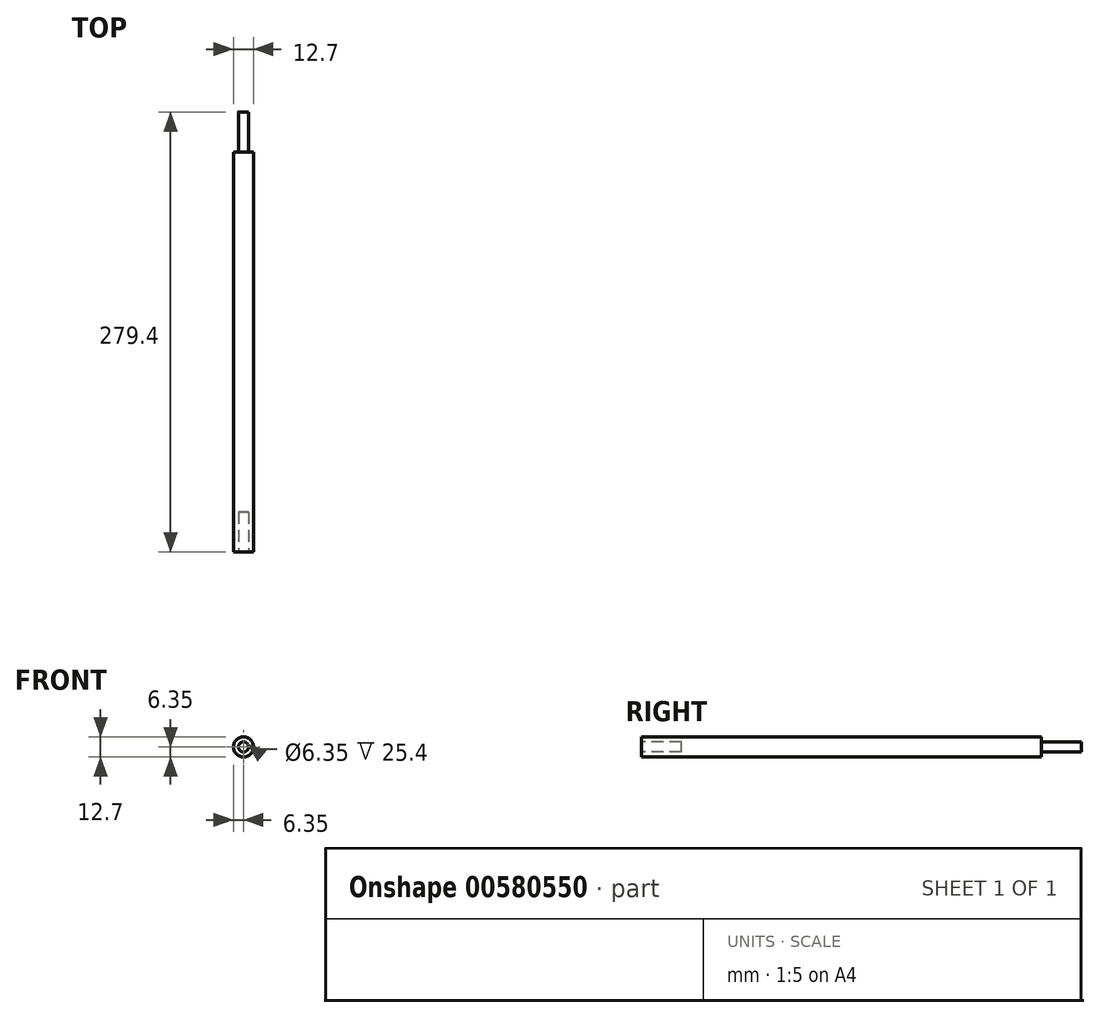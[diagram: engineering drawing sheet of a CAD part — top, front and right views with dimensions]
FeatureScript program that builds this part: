
annotation { "Feature Type Name" : "Feature", "Feature Type Description" : "" }
export const myFeature = defineFeature(function(context is Context, id is Id, definition is map)
    precondition{}
    {
        {
            var Q0;
            Q0=qCreatedBy(makeId("Front.planeOp"),FACE);
            var sketch = newSketch(context, id + "F0", { "sketchPlane" : qUnion([Q0])});
            skCircle(sketch, "E0", {"center": v(0, 0) * mm, "radius": 6.35 * mm});
            skSolve(sketch);
        }
        {
            var Q0;
            Q0=makeQuery(id+"F0.imprint","IMPRINT",FACE,{"disambiguationData":[TD([[makeQuery(id+"F0.imprint","IMPRINT",EDGE,{"derivedFrom":sQuery(id+"F0.wireOp",EDGE,"E0")}),1.0]])]});
            extrude(context, id + "F1", {"entities" : qUnion([Q0]), "depth" : 279.4 * mm, "offsetDistance" : 25.4 * mm});
        }
        {
            var Q0;
            Q0=makeQuery(id+"F1.opExtrude","CAP_FACE",FACE,{"disambiguationData":[OSD([sQuery(id+"F0.wireOp",EDGE,"E0")])],"isStart":false});
            var sketch = newSketch(context, id + "F2", { "sketchPlane" : qUnion([Q0])});
            skCircle(sketch, "E1", {"center": v(0, 0) * mm, "radius": 3.18 * mm});
            skSolve(sketch);
        }
        {
            var Q0;
            Q0=makeQuery(id+"F2.imprint","IMPRINT",FACE,{"disambiguationData":[TD([[makeQuery(id+"F2.imprint","IMPRINT",EDGE,{"derivedFrom":sQuery(id+"F2.wireOp",EDGE,"E1")}),1.0]])]});
            extrude(context, id + "F3", {"entities" : qUnion([Q0]), "operationType" : NewBodyOperationType.REMOVE, "oppositeDirection" : true, "depth" : 25.4 * mm, "offsetDistance" : 25.4 * mm});
        }
        {
            var Q0;
            Q0=makeQuery(id+"F1.opExtrude","CAP_FACE",FACE,{"disambiguationData":[OSD([sQuery(id+"F0.wireOp",EDGE,"E0")])],"isStart":true});
            var sketch = newSketch(context, id + "F4", { "sketchPlane" : qUnion([Q0])});
            skCircle(sketch, "E2", {"center": v(0, 0) * mm, "radius": 3.17 * mm});
            skSolve(sketch);
        }
        {
            var Q0;
            Q0=makeQuery(id+"F4.imprint","IMPRINT",FACE,{"disambiguationData":[TD([[makeQuery(id+"F4.imprint","IMPRINT",EDGE,{"derivedFrom":sQuery(id+"F4.wireOp",EDGE,"E2")}),-1.0]])]});
            extrude(context, id + "F5", {"entities" : qUnion([Q0]), "operationType" : NewBodyOperationType.REMOVE, "oppositeDirection" : true, "depth" : 25.4 * mm, "offsetDistance" : 25.4 * mm});
        }
    });
